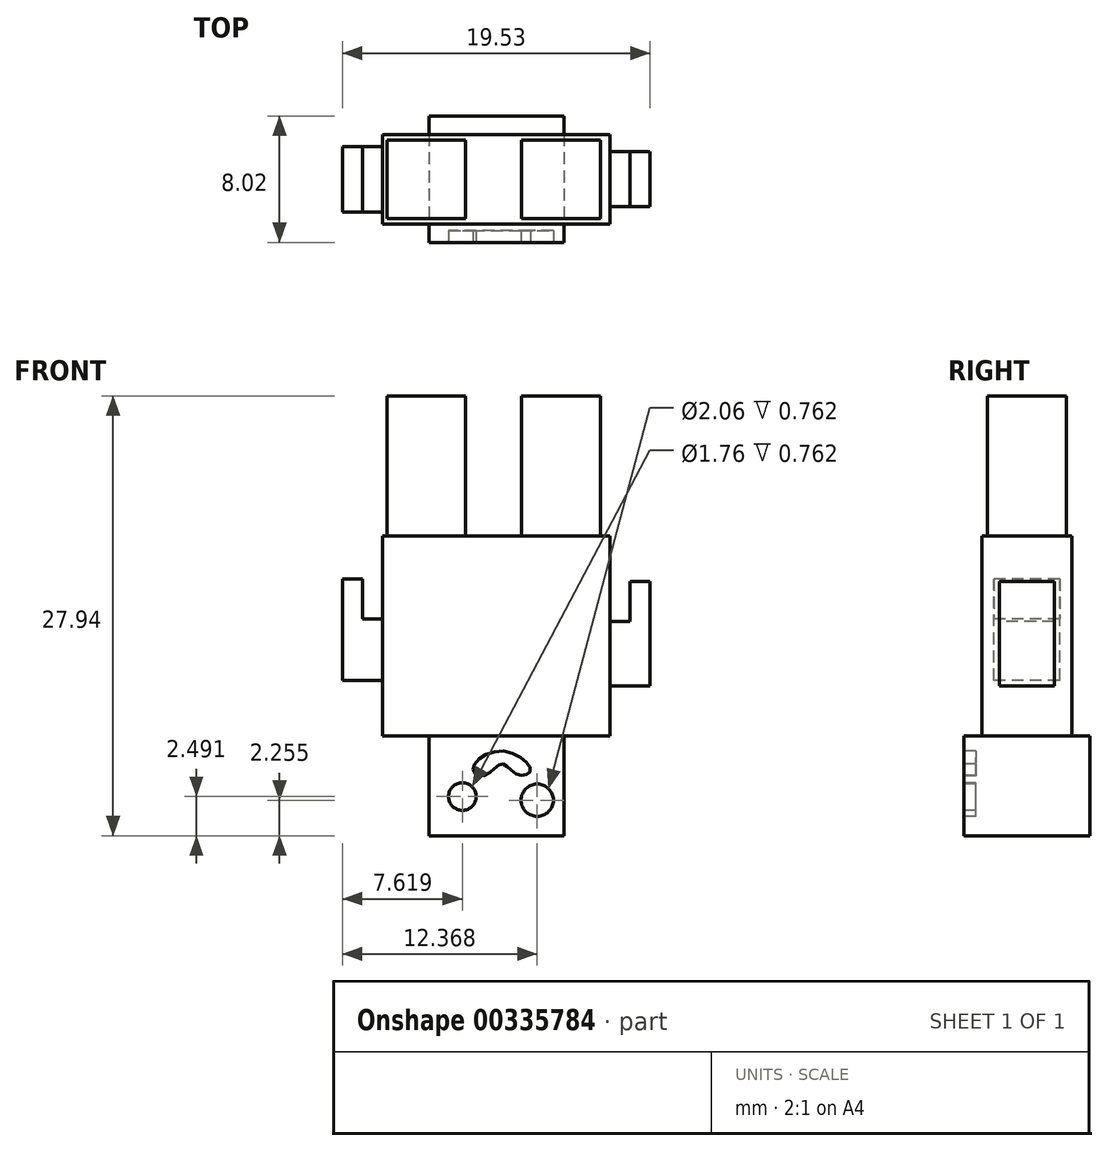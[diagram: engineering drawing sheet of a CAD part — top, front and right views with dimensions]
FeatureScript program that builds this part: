
annotation { "Feature Type Name" : "Feature", "Feature Type Description" : "" }
export const myFeature = defineFeature(function(context is Context, id is Id, definition is map)
    precondition{}
    {
        {
            var Q0;
            Q0=qCreatedBy(makeId("Top.planeOp"),FACE);
            var sketch = newSketch(context, id + "F0", { "sketchPlane" : qUnion([Q0])});
            skLineSegment(sketch, "E0.bottom", {"start": v(-5.08, -2.5) * mm, "end": v(-10.08, -2.5) * mm});
            skLineSegment(sketch, "E0.top", {"start": v(-5.08, 2.5) * mm, "end": v(-10.08, 2.5) * mm});
            skLineSegment(sketch, "E0.left", {"start": v(-5.08, -2.5) * mm, "end": v(-5.08, 2.5) * mm});
            skLineSegment(sketch, "E0.right", {"start": v(-10.08, -2.5) * mm, "end": v(-10.08, 2.5) * mm});
            skPoint(sketch, "E0.middle", {"position": v(-7.58, 0) * mm});
            skLineSegment(sketch, "E1.bottom", {"start": v(3.47, -2.5) * mm, "end": v(-1.53, -2.5) * mm});
            skLineSegment(sketch, "E1.top", {"start": v(3.47, 2.5) * mm, "end": v(-1.53, 2.5) * mm});
            skLineSegment(sketch, "E1.left", {"start": v(3.47, -2.5) * mm, "end": v(3.47, 2.5) * mm});
            skLineSegment(sketch, "E1.right", {"start": v(-1.53, -2.5) * mm, "end": v(-1.53, 2.5) * mm});
            skPoint(sketch, "E1.middle", {"position": v(0.97, 0) * mm});
            skSolve(sketch);
        }
        {
            var Q0;
            Q0=makeQuery(id+"F0.imprint","IMPRINT",FACE,{"disambiguationData":[TD([[makeQuery(id+"F0.imprint","IMPRINT",EDGE,{"derivedFrom":sQuery(id+"F0.wireOp",EDGE,"E0.bottom")}),-1.0]])]});
            var Q1;
            Q1=makeQuery(id+"F0.imprint","IMPRINT",FACE,{"disambiguationData":[TD([[makeQuery(id+"F0.imprint","IMPRINT",EDGE,{"derivedFrom":sQuery(id+"F0.wireOp",EDGE,"E1.bottom")}),-1.0]])]});
            extrude(context, id + "F1", {"entities" : qUnion([Q0, Q1]), "depth" : 8.9 * mm});
        }
        {
            var Q0;
            Q0=qCreatedBy(makeId("Top.planeOp"),FACE);
            var sketch = newSketch(context, id + "F2", { "sketchPlane" : qUnion([Q0])});
            skLineSegment(sketch, "E2.bottom", {"start": v(-10.37, -2.85) * mm, "end": v(4.08, -2.85) * mm});
            skLineSegment(sketch, "E2.top", {"start": v(-10.37, 2.85) * mm, "end": v(4.08, 2.85) * mm});
            skLineSegment(sketch, "E2.left", {"start": v(-10.37, -2.85) * mm, "end": v(-10.37, 2.85) * mm});
            skLineSegment(sketch, "E2.right", {"start": v(4.08, -2.85) * mm, "end": v(4.08, 2.85) * mm});
            skPoint(sketch, "E2.middle", {"position": v(-3.15, 0) * mm});
            skSolve(sketch);
        }
        {
            var Q0;
            Q0=makeQuery(id+"F2.imprint","IMPRINT",FACE,{"disambiguationData":[TD([[makeQuery(id+"F2.imprint","IMPRINT",EDGE,{"derivedFrom":sQuery(id+"F2.wireOp",EDGE,"E2.bottom")}),1.0]])]});
            extrude(context, id + "F3", {"entities" : qUnion([Q0]), "depth" : -12.7 * mm});
        }
        {
            var Q0;
            Q0=makeQuery(id+"F3.opExtrude","CAP_FACE",FACE,{"disambiguationData":[OSD([sQuery(id+"F2.wireOp",EDGE,"E2.bottom"),sQuery(id+"F2.wireOp",EDGE,"E2.top"),sQuery(id+"F2.wireOp",EDGE,"E2.left"),sQuery(id+"F2.wireOp",EDGE,"E2.right")])],"isStart":false});
            var sketch = newSketch(context, id + "F4", { "sketchPlane" : qUnion([Q0])});
            skLineSegment(sketch, "E3.bottom", {"start": v(-7.42, -4) * mm, "end": v(1.15, -4) * mm});
            skLineSegment(sketch, "E3.top", {"start": v(-7.42, 4) * mm, "end": v(1.15, 4) * mm});
            skLineSegment(sketch, "E3.left", {"start": v(-7.42, -4) * mm, "end": v(-7.42, 4) * mm});
            skLineSegment(sketch, "E3.right", {"start": v(1.15, -4) * mm, "end": v(1.15, 4) * mm});
            skPoint(sketch, "E3.middle", {"position": v(-3.14, 0) * mm});
            skSolve(sketch);
        }
        {
            var Q0;
            {var subQ0=sQuery(id+"F4.wireOp",EDGE,"E3.bottom");Q0=makeQuery(id+"F4.imprint","IMPRINT",FACE,{"disambiguationData":[TD([[makeQuery(id+"F4.imprint","IMPRINT",EDGE,{"derivedFrom":subQ0}),1.0]])]});}
            var Q1;
            {var subQ0=sQuery(id+"F4.wireOp",EDGE,"E3.top");Q1=makeQuery(id+"F4.imprint","IMPRINT",FACE,{"disambiguationData":[TD([[makeQuery(id+"F4.imprint","IMPRINT",EDGE,{"derivedFrom":subQ0}),-1.0]])]});}
            var Q2;
            {var subQ0=sQuery(id+"F4.wireOp",EDGE,"E3.left");var subQ1=makeQuery(id+"F3.opExtrude","CAP_EDGE",EDGE,{"disambiguationData":[OSD([sQuery(id+"F2.wireOp",EDGE,"E2.top")])],"isStart":false});var subQ2=makeQuery(id+"F4.imprint","INTERSECT",VERTEX,{"derivedFrom":[subQ1,subQ0]});Q2=makeQuery(id+"F4.imprint","IMPRINT",FACE,{"disambiguationData":[TD([[makeQuery(id+"F4.imprint","IMPRINT",EDGE,{"disambiguationData":[TD([[subQ2,-1.0]])],"derivedFrom":subQ0}),-1.0]])]});}
            extrude(context, id + "F5", {"entities" : qUnion([Q0, Q1, Q2]), "operationType" : NewBodyOperationType.ADD, "depth" : 6.35 * mm});
        }
        {
            var Q0;
            Q0=makeQuery(id+"F3.opExtrude","SWEPT_FACE",FACE,{"disambiguationData":[OSD([sQuery(id+"F2.wireOp",EDGE,"E2.right")])]});
            var sketch = newSketch(context, id + "F6", { "sketchPlane" : qUnion([Q0])});
            skLineSegment(sketch, "E4.bottom", {"start": v(1.74, -5.45) * mm, "end": v(-1.74, -5.45) * mm});
            skLineSegment(sketch, "E4.top", {"start": v(1.74, -9.53) * mm, "end": v(-1.74, -9.53) * mm});
            skLineSegment(sketch, "E4.left", {"start": v(1.74, -5.45) * mm, "end": v(1.74, -9.53) * mm});
            skLineSegment(sketch, "E4.right", {"start": v(-1.74, -5.45) * mm, "end": v(-1.74, -9.53) * mm});
            skPoint(sketch, "E4.middle", {"position": v(0, -7.49) * mm});
            skSolve(sketch);
        }
        {
            var Q0;
            Q0=makeQuery(id+"F6.imprint","IMPRINT",FACE,{"disambiguationData":[TD([[makeQuery(id+"F6.imprint","IMPRINT",EDGE,{"derivedFrom":sQuery(id+"F6.wireOp",EDGE,"E4.bottom")}),1.0]])]});
            extrude(context, id + "F7", {"entities" : qUnion([Q0]), "operationType" : NewBodyOperationType.ADD, "depth" : 2.54 * mm});
        }
        {
            var Q0;
            Q0=makeQuery(id+"F3.opExtrude","SWEPT_FACE",FACE,{"disambiguationData":[OSD([sQuery(id+"F2.wireOp",EDGE,"E2.left")])]});
            var sketch = newSketch(context, id + "F8", { "sketchPlane" : qUnion([Q0])});
            skLineSegment(sketch, "E5.bottom", {"start": v(-2.08, -9.19) * mm, "end": v(2.08, -9.19) * mm});
            skLineSegment(sketch, "E5.top", {"start": v(-2.08, -5.28) * mm, "end": v(2.08, -5.28) * mm});
            skLineSegment(sketch, "E5.left", {"start": v(-2.08, -9.19) * mm, "end": v(-2.08, -5.28) * mm});
            skLineSegment(sketch, "E5.right", {"start": v(2.08, -9.19) * mm, "end": v(2.08, -5.28) * mm});
            skPoint(sketch, "E5.middle", {"position": v(0, -7.24) * mm});
            skSolve(sketch);
        }
        {
            var Q0;
            Q0=makeQuery(id+"F8.imprint","IMPRINT",FACE,{"disambiguationData":[TD([[makeQuery(id+"F8.imprint","IMPRINT",EDGE,{"derivedFrom":sQuery(id+"F8.wireOp",EDGE,"E5.bottom")}),1.0]])]});
            extrude(context, id + "F9", {"entities" : qUnion([Q0]), "operationType" : NewBodyOperationType.ADD, "depth" : 2.54 * mm});
        }
        {
            var Q0;
            Q0=makeQuery(id+"F9.opExtrude","SWEPT_FACE",FACE,{"disambiguationData":[OSD([sQuery(id+"F8.wireOp",EDGE,"E5.top")])]});
            var sketch = newSketch(context, id + "F10", { "sketchPlane" : qUnion([Q0])});
            skLineSegment(sketch, "E6.bottom", {"start": v(-12.9, -2.08) * mm, "end": v(-11.64, -2.08) * mm});
            skLineSegment(sketch, "E6.top", {"start": v(-12.9, 2.08) * mm, "end": v(-11.64, 2.08) * mm});
            skLineSegment(sketch, "E6.left", {"start": v(-12.9, -2.08) * mm, "end": v(-12.9, 2.08) * mm});
            skLineSegment(sketch, "E6.right", {"start": v(-11.64, -2.08) * mm, "end": v(-11.64, 2.08) * mm});
            skSolve(sketch);
        }
        {
            var Q0;
            Q0=makeQuery(id+"F7.opExtrude","SWEPT_FACE",FACE,{"disambiguationData":[OSD([sQuery(id+"F6.wireOp",EDGE,"E4.bottom")])]});
            var sketch = newSketch(context, id + "F11", { "sketchPlane" : qUnion([Q0])});
            skLineSegment(sketch, "E7.bottom", {"start": v(6.62, -1.74) * mm, "end": v(5.35, -1.74) * mm});
            skLineSegment(sketch, "E7.top", {"start": v(6.62, 1.74) * mm, "end": v(5.35, 1.74) * mm});
            skLineSegment(sketch, "E7.left", {"start": v(6.62, -1.74) * mm, "end": v(6.62, 1.74) * mm});
            skLineSegment(sketch, "E7.right", {"start": v(5.35, -1.74) * mm, "end": v(5.35, 1.74) * mm});
            skSolve(sketch);
        }
        {
            var Q0;
            Q0=makeQuery(id+"F11.imprint","IMPRINT",FACE,{"disambiguationData":[TD([[makeQuery(id+"F11.imprint","IMPRINT",EDGE,{"derivedFrom":sQuery(id+"F11.wireOp",EDGE,"E7.bottom")}),-1.0]])]});
            var Q1;
            Q1=makeQuery(id+"F10.imprint","IMPRINT",FACE,{"disambiguationData":[TD([[makeQuery(id+"F10.imprint","IMPRINT",EDGE,{"derivedFrom":sQuery(id+"F10.wireOp",EDGE,"E6.bottom")}),1.0]])]});
            extrude(context, id + "F12", {"entities" : qUnion([Q0, Q1]), "operationType" : NewBodyOperationType.ADD, "depth" : 2.54 * mm});
        }
        {
            var Q0;
            Q0=makeQuery(id+"F5.opExtrude","SWEPT_FACE",FACE,{"disambiguationData":[OSD([sQuery(id+"F4.wireOp",EDGE,"E3.top")])]});
            var sketch = newSketch(context, id + "F13", { "sketchPlane" : qUnion([Q0])});
            skCircle(sketch, "E8", {"center": v(-0.54, -16.8) * mm, "radius": 1.03 * mm});
            skCircle(sketch, "E9", {"center": v(-5.3, -16.56) * mm, "radius": 0.88 * mm});
            skFitSpline(sketch, "E10", {"points": [v(-4.62, -14.83) * mm, v(-2.81, -13.67) * mm, v(-0.97, -14.9) * mm, v(-1.77, -15.17) * mm, v(-2.79, -14.49) * mm, v(-3.87, -15.22) * mm, v(-4.62, -14.83) * mm]});
            skSolve(sketch);
        }
        {
            var Q0;
            Q0=makeQuery(id+"F13.imprint","IMPRINT",FACE,{"disambiguationData":[TD([[makeQuery(id+"F13.imprint","IMPRINT",EDGE,{"derivedFrom":sQuery(id+"F13.wireOp",EDGE,"E8")}),1.0]])]});
            var Q1;
            Q1=makeQuery(id+"F13.imprint","IMPRINT",FACE,{"disambiguationData":[TD([[makeQuery(id+"F13.imprint","IMPRINT",EDGE,{"derivedFrom":sQuery(id+"F13.wireOp",EDGE,"E9")}),1.0]])]});
            var Q2;
            Q2=makeQuery(id+"F13.imprint","IMPRINT",FACE,{"disambiguationData":[TD([[makeQuery(id+"F13.imprint","IMPRINT",EDGE,{"derivedFrom":sQuery(id+"F13.wireOp",EDGE,"E10")}),-1.0]])]});
            extrude(context, id + "F14", {"entities" : qUnion([Q0, Q1, Q2]), "operationType" : NewBodyOperationType.REMOVE, "oppositeDirection" : true, "depth" : 0.76 * mm});
        }
    });
